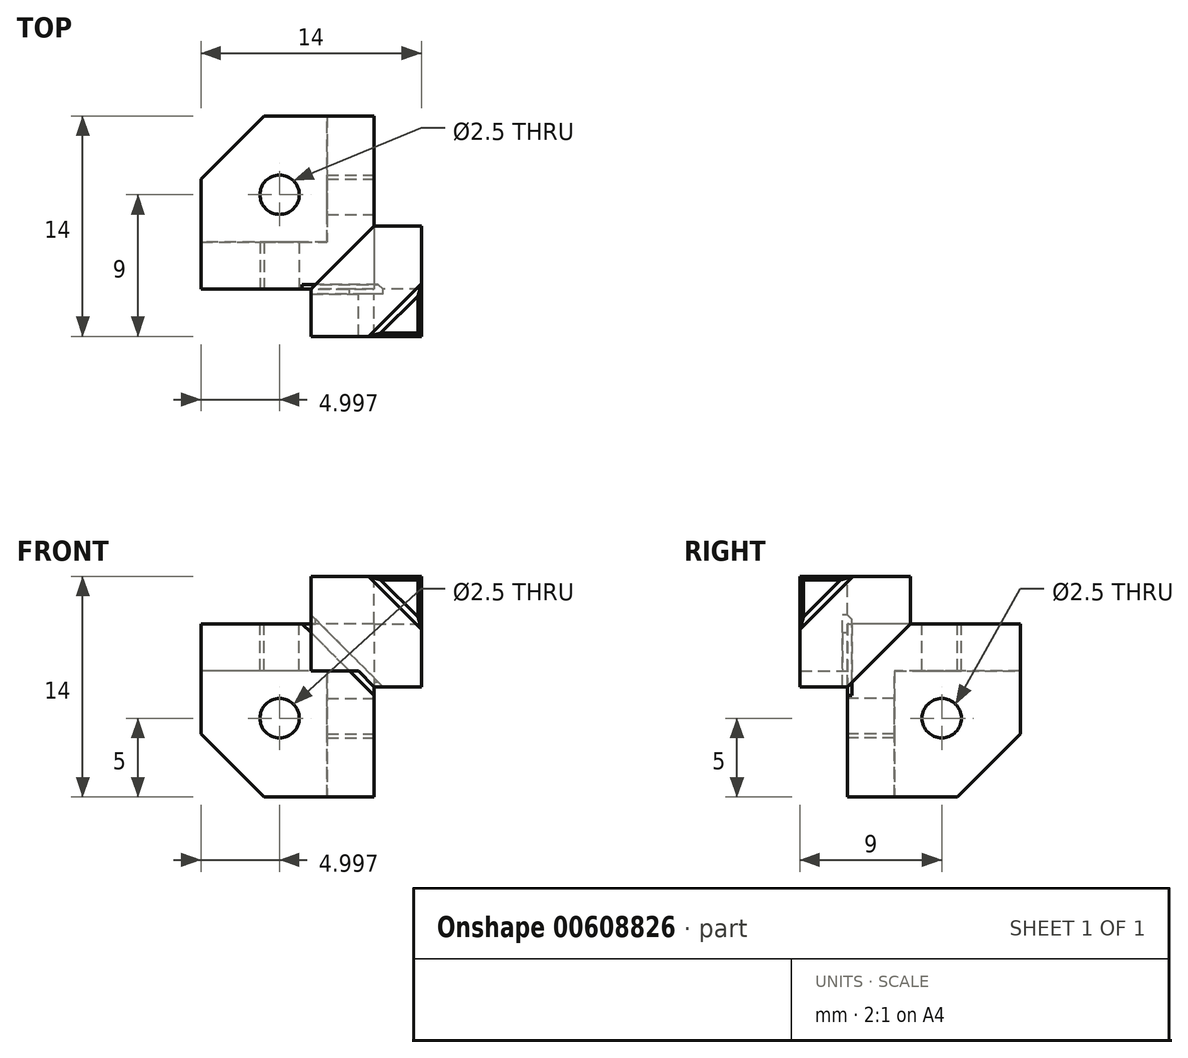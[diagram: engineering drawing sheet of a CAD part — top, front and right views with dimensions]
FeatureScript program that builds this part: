
annotation { "Feature Type Name" : "Feature", "Feature Type Description" : "" }
export const myFeature = defineFeature(function(context is Context, id is Id, definition is map)
    precondition{}
    {
        {
            var Q0;
            Q0=qCreatedBy(makeId("Front.planeOp"),FACE);
            var sketch = newSketch(context, id + "F0", { "sketchPlane" : qUnion([Q0])});
            skLineSegment(sketch, "E0", {"start": v(7.23, 36.22) * mm, "end": v(14.23, 36.22) * mm});
            skLineSegment(sketch, "E1", {"start": v(14.23, 36.22) * mm, "end": v(14.23, 29.22) * mm});
            skLineSegment(sketch, "E2", {"start": v(14.23, 29.22) * mm, "end": v(11.23, 29.22) * mm});
            skLineSegment(sketch, "E3", {"start": v(11.23, 29.22) * mm, "end": v(7.23, 33.22) * mm});
            skLineSegment(sketch, "E4", {"start": v(7.23, 33.22) * mm, "end": v(7.23, 36.22) * mm});
            skLineSegment(sketch, "E5", {"start": v(14.23, 29.22) * mm, "end": v(14.23, 27.22) * mm, "construction": true});
            skLineSegment(sketch, "E6", {"start": v(14.23, 27.22) * mm, "end": v(5.23, 27.22) * mm, "construction": true});
            skCircle(sketch, "E7", {"center": v(5.23, 27.22) * mm, "radius": 1.25 * mm});
            skLineSegment(sketch, "E8", {"start": v(7.23, 36.22) * mm, "end": v(0.23, 36.22) * mm});
            skLineSegment(sketch, "E9", {"start": v(0.23, 36.22) * mm, "end": v(0.23, 26.22) * mm});
            skLineSegment(sketch, "E10", {"start": v(0.23, 26.22) * mm, "end": v(4.23, 22.22) * mm});
            skLineSegment(sketch, "E11", {"start": v(4.23, 22.22) * mm, "end": v(14.23, 22.22) * mm});
            skLineSegment(sketch, "E12", {"start": v(14.23, 22.22) * mm, "end": v(14.23, 29.22) * mm});
            skSolve(sketch);
        }
        {
            var Q0;
            Q0=makeQuery(id+"F0.imprint","IMPRINT",FACE,{"disambiguationData":[TD([[makeQuery(id+"F0.imprint","IMPRINT",EDGE,{"derivedFrom":sQuery(id+"F0.wireOp",EDGE,"E0")}),-1.0]])]});
            extrude(context, id + "F1", {"entities" : qUnion([Q0]), "depth" : 3 * mm, "offsetDistance" : 25 * mm});
        }
        {
            var Q0;
            Q0=makeQuery(id+"F0.imprint","IMPRINT",FACE,{"disambiguationData":[TD([[makeQuery(id+"F0.imprint","IMPRINT",EDGE,{"derivedFrom":sQuery(id+"F0.wireOp",EDGE,"E2")}),1.0]])]});
            var Q1;
            Q1=makeQuery(id+"F0.imprint","IMPRINT",FACE,{"disambiguationData":[TD([[makeQuery(id+"F0.imprint","IMPRINT",EDGE,{"derivedFrom":sQuery(id+"F0.wireOp",EDGE,"E0")}),-1.0]])]});
            extrude(context, id + "F2", {"entities" : qUnion([Q0, Q1]), "operationType" : NewBodyOperationType.ADD, "oppositeDirection" : true, "depth" : 3 * mm, "offsetDistance" : 25 * mm});
        }
        {
            var Q0;
            {var subQ0=sQuery(id+"F0.wireOp",EDGE,"E0");Q0=makeQuery(id+"F2.boolean.opBoolean","MERGE",FACE,{"derivedFrom":[makeQuery(id+"F1.opExtrude","SWEPT_FACE",FACE,{"disambiguationData":[OSD([subQ0])]}),makeQuery(id+"F2.opExtrude","SWEPT_FACE",FACE,{"disambiguationData":[OSD([subQ0,sQuery(id+"F0.wireOp",EDGE,"E8")])]})]});}
            var sketch = newSketch(context, id + "F3", { "sketchPlane" : qUnion([Q0])});
            skLineSegment(sketch, "E13", {"start": v(7.23, -3) * mm, "end": v(14.23, -3) * mm});
            skLineSegment(sketch, "E14", {"start": v(14.23, -3) * mm, "end": v(14.23, 4) * mm});
            skLineSegment(sketch, "E15", {"start": v(14.23, 4) * mm, "end": v(11.23, 4) * mm});
            skLineSegment(sketch, "E16", {"start": v(11.23, 4) * mm, "end": v(7.23, 0) * mm});
            skLineSegment(sketch, "E17", {"start": v(11.23, 4) * mm, "end": v(11.23, 11) * mm});
            skLineSegment(sketch, "E18", {"start": v(11.23, 11) * mm, "end": v(4.23, 11) * mm});
            skLineSegment(sketch, "E19", {"start": v(4.23, 11) * mm, "end": v(0.23, 7) * mm});
            skPoint(sketch, "E19.endSnap0", {"position": v(0.23, 1.5) * mm});
            skLineSegment(sketch, "E20", {"start": v(0.23, 7) * mm, "end": v(0.23, 0) * mm});
            skLineSegment(sketch, "E21", {"start": v(7.02, -3) * mm, "end": v(5.23, -3) * mm, "construction": true});
            skLineSegment(sketch, "E22", {"start": v(5.23, -3) * mm, "end": v(5.23, 6) * mm, "construction": true});
            skCircle(sketch, "E23", {"center": v(5.23, 6) * mm, "radius": 1.25 * mm});
            skSolve(sketch);
        }
        {
            var Q0;
            {var subQ1=sQuery(id+"F3.wireOp",EDGE,"E17");Q0=makeQuery(id+"F3.imprint","IMPRINT",FACE,{"disambiguationData":[TD([[makeQuery(id+"F3.imprint","IMPRINT",EDGE,{"derivedFrom":subQ1}),1.0]])]});}
            var Q1;
            {var subQ3=sQuery(id+"F3.wireOp",EDGE,"E15");Q1=makeQuery(id+"F3.imprint","IMPRINT",FACE,{"disambiguationData":[TD([[makeQuery(id+"F3.imprint","IMPRINT",EDGE,{"derivedFrom":subQ3}),1.0]])]});}
            extrude(context, id + "F4", {"entities" : qUnion([Q0, Q1]), "operationType" : NewBodyOperationType.ADD, "oppositeDirection" : true, "depth" : 6 * mm, "offsetDistance" : 25 * mm});
        }
        {
            var Q0;
            {var subQ1=sQuery(id+"F3.wireOp",EDGE,"E17");Q0=makeQuery(id+"F3.imprint","IMPRINT",FACE,{"disambiguationData":[TD([[makeQuery(id+"F3.imprint","IMPRINT",EDGE,{"derivedFrom":subQ1}),1.0]])]});}
            var Q1;
            {var subQ1=sQuery(id+"F0.wireOp",EDGE,"E8");var subQ2=sQuery(id+"F0.wireOp",EDGE,"E0");var subQ3=makeQuery(id+"F2.opExtrude","CAP_EDGE",EDGE,{"disambiguationData":[OSD([subQ2,subQ1])],"isStart":true});Q1=makeQuery(id+"F3.imprint","IMPRINT",FACE,{"disambiguationData":[TD([[makeQuery(id+"F3.imprint","IMPRINT",EDGE,{"derivedFrom":subQ3}),-1.0]])]});}
            extrude(context, id + "F5", {"entities" : qUnion([Q0, Q1]), "operationType" : NewBodyOperationType.REMOVE, "oppositeDirection" : true, "depth" : 3 * mm, "offsetDistance" : 25 * mm});
        }
        {
            var Q0;
            {var subQ0=sQuery(id+"F0.wireOp",EDGE,"E1");Q0=makeQuery(id+"F2.boolean.opBoolean","MERGE",FACE,{"derivedFrom":[makeQuery(id+"F1.opExtrude","SWEPT_FACE",FACE,{"disambiguationData":[OSD([subQ0])]}),makeQuery(id+"F2.opExtrude","SWEPT_FACE",FACE,{"disambiguationData":[OSD([subQ0,sQuery(id+"F0.wireOp",EDGE,"E12")])]})]});}
            var sketch = newSketch(context, id + "F6", { "sketchPlane" : qUnion([Q0])});
            skLineSegment(sketch, "E24", {"start": v(0, 29.22) * mm, "end": v(0, 22.22) * mm});
            skLineSegment(sketch, "E25", {"start": v(0, 22.22) * mm, "end": v(7, 22.22) * mm});
            skLineSegment(sketch, "E26", {"start": v(11, 33.22) * mm, "end": v(11, 26.22) * mm});
            skLineSegment(sketch, "E27", {"start": v(11, 26.22) * mm, "end": v(7, 22.22) * mm});
            skLineSegment(sketch, "E28", {"start": v(-3, 29.22) * mm, "end": v(-3, 27.22) * mm, "construction": true});
            skLineSegment(sketch, "E29", {"start": v(-3, 27.22) * mm, "end": v(6, 27.22) * mm, "construction": true});
            skCircle(sketch, "E30", {"center": v(6, 27.22) * mm, "radius": 1.25 * mm});
            skLineSegment(sketch, "E31", {"start": v(11, 33.22) * mm, "end": v(4, 33.22) * mm});
            skLineSegment(sketch, "E32", {"start": v(4, 33.22) * mm, "end": v(0, 29.22) * mm});
            skSolve(sketch);
        }
        {
            var Q0;
            Q0=qSketchRegion(id+"F6",true);
            extrude(context, id + "F7", {"entities" : qUnion([Q0]), "operationType" : NewBodyOperationType.ADD, "oppositeDirection" : true, "depth" : 6 * mm, "offsetDistance" : 25 * mm});
        }
        {
            var Q0;
            {var subQ2=sQuery(id+"F6.wireOp",EDGE,"E24");Q0=makeQuery(id+"F6.imprint","IMPRINT",FACE,{"disambiguationData":[TD([[makeQuery(id+"F6.imprint","IMPRINT",EDGE,{"derivedFrom":subQ2}),-1.0]])]});}
            var Q1;
            Q1=makeQuery(id+"F6.imprint","IMPRINT",FACE,{"disambiguationData":[TD([[makeQuery(id+"F6.imprint","IMPRINT",EDGE,{"derivedFrom":sQuery(id+"F6.wireOp",EDGE,"E26")}),-1.0]])]});
            extrude(context, id + "F8", {"entities" : qUnion([Q0, Q1]), "operationType" : NewBodyOperationType.REMOVE, "oppositeDirection" : true, "depth" : 3 * mm, "offsetDistance" : 25 * mm});
        }
        {
            var Q0;
            Q0=makeQuery(id+"F1.opExtrude","CAP_FACE",FACE,{"disambiguationData":[OSD([sQuery(id+"F0.wireOp",EDGE,"E0"),sQuery(id+"F0.wireOp",EDGE,"E1"),sQuery(id+"F0.wireOp",EDGE,"E2"),sQuery(id+"F0.wireOp",EDGE,"E3"),sQuery(id+"F0.wireOp",EDGE,"E4")])],"isStart":false});
            var sketch = newSketch(context, id + "F9", { "sketchPlane" : qUnion([Q0])});
            skLineSegment(sketch, "E33", {"start": v(14.23, 36.22) * mm, "end": v(14.23, 33.22) * mm});
            skLineSegment(sketch, "E34", {"start": v(14.23, 33.22) * mm, "end": v(11.23, 36.22) * mm});
            skLineSegment(sketch, "E35", {"start": v(11.23, 36.22) * mm, "end": v(14.23, 36.22) * mm});
            skSolve(sketch);
        }
        {
            var Q0;
            Q0=makeQuery(id+"F9.imprint","IMPRINT",FACE,{"disambiguationData":[TD([[makeQuery(id+"F9.imprint","IMPRINT",EDGE,{"derivedFrom":sQuery(id+"F9.wireOp",EDGE,"E33")}),-1.0]])]});
            extrude(context, id + "F10", {"entities" : qUnion([Q0]), "operationType" : NewBodyOperationType.REMOVE, "oppositeDirection" : true, "depth" : 3 * mm, "offsetDistance" : 25 * mm});
        }
        {
            var Q0;
            Q0=makeQuery(id+"F10.boolean.opBoolean","COPY",EDGE,{"derivedFrom":makeQuery(id+"F10.opExtrude","CAP_EDGE",EDGE,{"disambiguationData":[OSD([sQuery(id+"F9.wireOp",EDGE,"E34")])],"isStart":false})});
            chamfer(context, id + "F11", {"entities" : qUnion([Q0]), "chamferType" : ChamferType.OFFSET_ANGLE, "width" : 3 * mm, "oppositeDirection" : false, "angle" : 35.4 * degree, "tangentPropagation" : true});
        }
        {
            var Q0;
            Q0=makeQuery(id+"F11.opChamfer","BLEND_EDGE",EDGE,{"blendedFrom":[makeQuery(id+"F10.boolean.opBoolean","COPY",EDGE,{"derivedFrom":makeQuery(id+"F10.opExtrude","CAP_EDGE",EDGE,{"disambiguationData":[OSD([sQuery(id+"F9.wireOp",EDGE,"E34")])],"isStart":false})}),makeQuery(id+"F1.opExtrude","CAP_FACE",FACE,{"disambiguationData":[OSD([sQuery(id+"F0.wireOp",EDGE,"E0"),sQuery(id+"F0.wireOp",EDGE,"E1"),sQuery(id+"F0.wireOp",EDGE,"E2"),sQuery(id+"F0.wireOp",EDGE,"E3"),sQuery(id+"F0.wireOp",EDGE,"E4")])],"isStart":false})],"blendedInto":[makeQuery(id+"F1.opExtrude","CAP_FACE",FACE,{"disambiguationData":[OSD([sQuery(id+"F0.wireOp",EDGE,"E0"),sQuery(id+"F0.wireOp",EDGE,"E1"),sQuery(id+"F0.wireOp",EDGE,"E2"),sQuery(id+"F0.wireOp",EDGE,"E3"),sQuery(id+"F0.wireOp",EDGE,"E4")])],"isStart":false})]});
            var Q1;
            {var subQ0=sQuery(id+"F0.wireOp",EDGE,"E8");var subQ1=sQuery(id+"F0.wireOp",EDGE,"E0");Q1=makeQuery(id+"F11.opChamfer","BLEND_EDGE",EDGE,{"blendedFrom":[makeQuery(id+"F10.boolean.opBoolean","COPY",EDGE,{"derivedFrom":makeQuery(id+"F10.opExtrude","CAP_EDGE",EDGE,{"disambiguationData":[OSD([sQuery(id+"F9.wireOp",EDGE,"E34")])],"isStart":false})}),makeQuery(id+"F4.boolean.opBoolean","MERGE",FACE,{"derivedFrom":[makeQuery(id+"F2.boolean.opBoolean","MERGE",FACE,{"derivedFrom":[makeQuery(id+"F1.opExtrude","SWEPT_FACE",FACE,{"disambiguationData":[OSD([subQ1])]}),makeQuery(id+"F2.opExtrude","SWEPT_FACE",FACE,{"disambiguationData":[OSD([subQ1,subQ0])]})]}),makeQuery(id+"F4.opExtrude","CAP_FACE",FACE,{"disambiguationData":[OSD([subQ1,subQ0,sQuery(id+"F3.wireOp",EDGE,"id0TNCpU-tjdV-AgSU-QIlH-1rNdUmwGPP8J"),sQuery(id+"F3.wireOp",EDGE,"mGFVvrbr-tIrU-syV4-yza1-VgwdehKtnJvE"),sQuery(id+"F3.wireOp",EDGE,"wSTTxPhp-j6Tf-tGPT-JtDE-c5HYP9l80gTy"),sQuery(id+"F3.wireOp",EDGE,"6f74HBZF-W9bh-Bztp-LMnC-ap8Q1K5RPxhI"),sQuery(id+"F3.wireOp",EDGE,"pXlPqK1o-hzZR-9fDG-u2KL-nj3FlQz3lFwb")])],"isStart":true})]})],"blendedInto":[makeQuery(id+"F4.boolean.opBoolean","MERGE",FACE,{"derivedFrom":[makeQuery(id+"F2.boolean.opBoolean","MERGE",FACE,{"derivedFrom":[makeQuery(id+"F1.opExtrude","SWEPT_FACE",FACE,{"disambiguationData":[OSD([subQ1])]}),makeQuery(id+"F2.opExtrude","SWEPT_FACE",FACE,{"disambiguationData":[OSD([subQ1,subQ0])]})]}),makeQuery(id+"F4.opExtrude","CAP_FACE",FACE,{"disambiguationData":[OSD([subQ1,subQ0,sQuery(id+"F3.wireOp",EDGE,"id0TNCpU-tjdV-AgSU-QIlH-1rNdUmwGPP8J"),sQuery(id+"F3.wireOp",EDGE,"mGFVvrbr-tIrU-syV4-yza1-VgwdehKtnJvE"),sQuery(id+"F3.wireOp",EDGE,"wSTTxPhp-j6Tf-tGPT-JtDE-c5HYP9l80gTy"),sQuery(id+"F3.wireOp",EDGE,"6f74HBZF-W9bh-Bztp-LMnC-ap8Q1K5RPxhI"),sQuery(id+"F3.wireOp",EDGE,"pXlPqK1o-hzZR-9fDG-u2KL-nj3FlQz3lFwb")])],"isStart":true})]})]});}
            var Q2;
            {var subQ0=sQuery(id+"F0.wireOp",EDGE,"E1");Q2=makeQuery(id+"F11.opChamfer","BLEND_EDGE",EDGE,{"blendedFrom":[makeQuery(id+"F10.boolean.opBoolean","COPY",EDGE,{"derivedFrom":makeQuery(id+"F10.opExtrude","CAP_EDGE",EDGE,{"disambiguationData":[OSD([sQuery(id+"F9.wireOp",EDGE,"E34")])],"isStart":false})}),makeQuery(id+"F7.boolean.opBoolean","MERGE",FACE,{"derivedFrom":[makeQuery(id+"F2.boolean.opBoolean","MERGE",FACE,{"derivedFrom":[makeQuery(id+"F1.opExtrude","SWEPT_FACE",FACE,{"disambiguationData":[OSD([subQ0])]}),makeQuery(id+"F2.opExtrude","SWEPT_FACE",FACE,{"disambiguationData":[OSD([subQ0,sQuery(id+"F0.wireOp",EDGE,"E12")])]})]}),makeQuery(id+"F7.opExtrude","CAP_FACE",FACE,{"disambiguationData":[OSD([sQuery(id+"F6.wireOp",EDGE,"bjqw6rF1-9aoZ-1MRt-8oHp-ZjFiTM0oOFLL"),sQuery(id+"F6.wireOp",EDGE,"E24"),sQuery(id+"F6.wireOp",EDGE,"E25"),sQuery(id+"F6.wireOp",EDGE,"4vnc1qx3-YKp5-J8BV-yxKJ-AHBmvpOXDA1h"),sQuery(id+"F6.wireOp",EDGE,"E26"),sQuery(id+"F6.wireOp",EDGE,"E27"),sQuery(id+"F6.wireOp",EDGE,"E30")])],"isStart":true})]})],"blendedInto":[makeQuery(id+"F7.boolean.opBoolean","MERGE",FACE,{"derivedFrom":[makeQuery(id+"F2.boolean.opBoolean","MERGE",FACE,{"derivedFrom":[makeQuery(id+"F1.opExtrude","SWEPT_FACE",FACE,{"disambiguationData":[OSD([subQ0])]}),makeQuery(id+"F2.opExtrude","SWEPT_FACE",FACE,{"disambiguationData":[OSD([subQ0,sQuery(id+"F0.wireOp",EDGE,"E12")])]})]}),makeQuery(id+"F7.opExtrude","CAP_FACE",FACE,{"disambiguationData":[OSD([sQuery(id+"F6.wireOp",EDGE,"bjqw6rF1-9aoZ-1MRt-8oHp-ZjFiTM0oOFLL"),sQuery(id+"F6.wireOp",EDGE,"E24"),sQuery(id+"F6.wireOp",EDGE,"E25"),sQuery(id+"F6.wireOp",EDGE,"4vnc1qx3-YKp5-J8BV-yxKJ-AHBmvpOXDA1h"),sQuery(id+"F6.wireOp",EDGE,"E26"),sQuery(id+"F6.wireOp",EDGE,"E27"),sQuery(id+"F6.wireOp",EDGE,"E30")])],"isStart":true})]})]});}
            chamfer(context, id + "F12", {"entities" : qUnion([Q0, Q1, Q2]), "width" : .5 * mm, "tangentPropagation" : true});
        }
        {
            var Q0;
            Q0=makeQuery(id+"F2.opExtrude","CAP_FACE",FACE,{"disambiguationData":[OSD([sQuery(id+"F0.wireOp",EDGE,"E0"),sQuery(id+"F0.wireOp",EDGE,"E1"),sQuery(id+"F0.wireOp",EDGE,"E7"),sQuery(id+"F0.wireOp",EDGE,"E8"),sQuery(id+"F0.wireOp",EDGE,"E9"),sQuery(id+"F0.wireOp",EDGE,"E10"),sQuery(id+"F0.wireOp",EDGE,"E11"),sQuery(id+"F0.wireOp",EDGE,"E12")])],"isStart":true});
            var sketch = newSketch(context, id + "F13", { "sketchPlane" : qUnion([Q0])});
            skLineSegment(sketch, "E36", {"start": v(6.25, 33.63) * mm, "end": v(11.72, 28.17) * mm});
            skLineSegment(sketch, "E37", {"start": v(11.72, 28.17) * mm, "end": v(11.23, 28.17) * mm, "construction": true});
            skLineSegment(sketch, "E38", {"start": v(11.72, 28.17) * mm, "end": v(12.28, 28.73) * mm});
            skLineSegment(sketch, "E39", {"start": v(12.28, 28.73) * mm, "end": v(6.82, 34.2) * mm});
            skLineSegment(sketch, "E40", {"start": v(6.82, 34.2) * mm, "end": v(6.25, 33.63) * mm});
            skLineSegment(sketch, "E41", {"start": v(9.83, 30.62) * mm, "end": v(9.55, 30.33) * mm, "construction": true});
            skLineSegment(sketch, "E42", {"start": v(9.83, 30.62) * mm, "end": v(10.11, 30.9) * mm, "construction": true});
            skSolve(sketch);
        }
        {
            var Q0;
            Q0 = qSketchRegion(id + "F13", true);
            extrude(context, id + "F14", {"entities" : qUnion([Q0]), "operationType" : NewBodyOperationType.REMOVE, "endBound" : BoundingType.SYMMETRIC, "depth" : .6 * mm, "offsetDistance" : 25 * mm});
        }
    });
